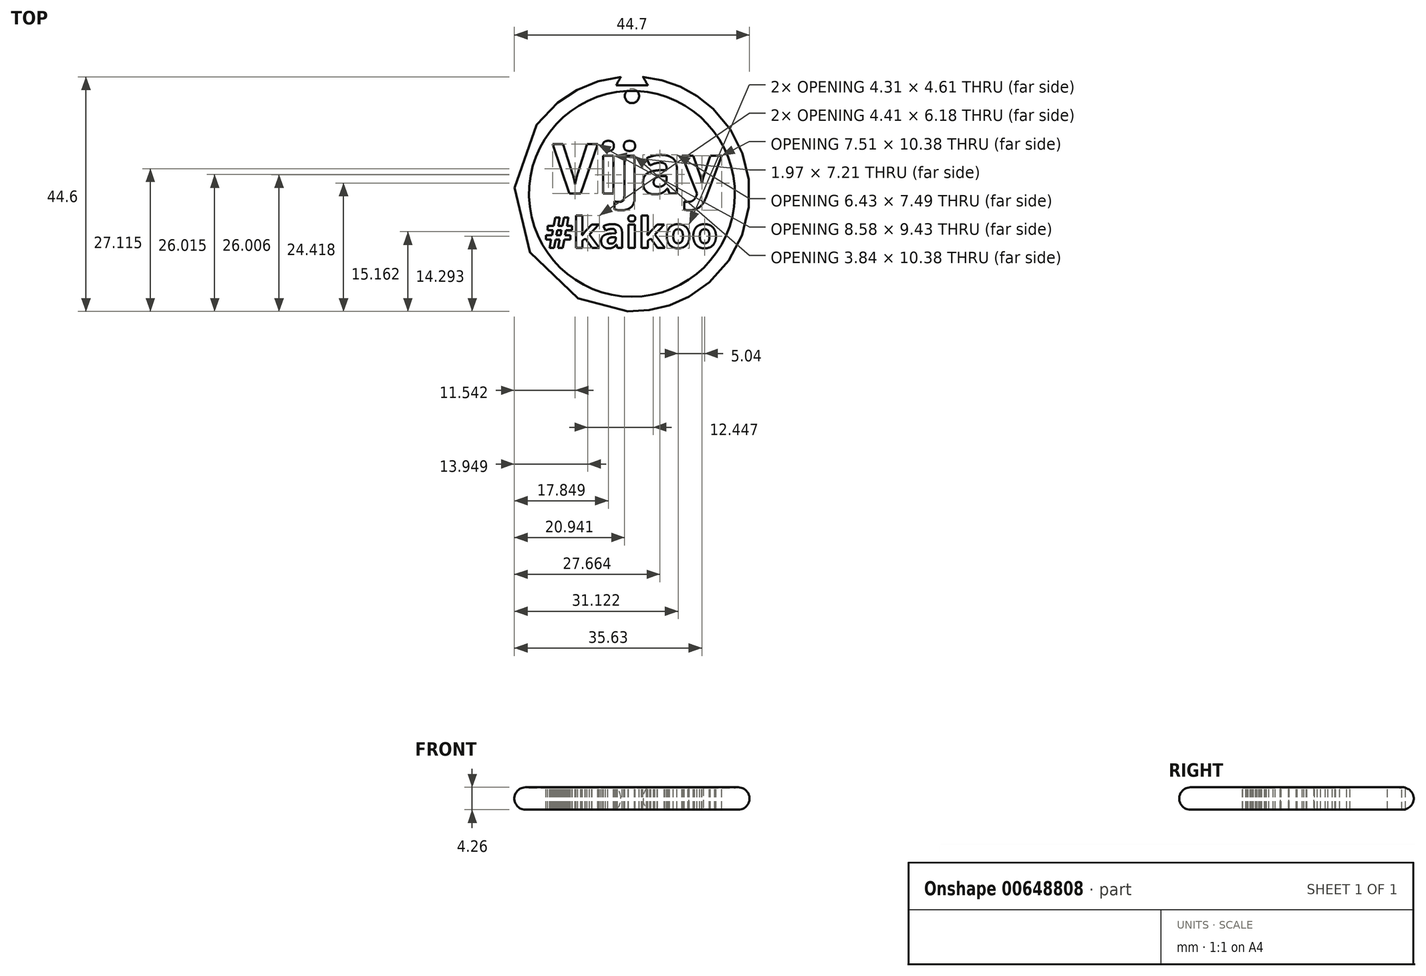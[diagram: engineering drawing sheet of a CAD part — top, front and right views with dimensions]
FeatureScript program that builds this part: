
annotation { "Feature Type Name" : "Feature", "Feature Type Description" : "" }
export const myFeature = defineFeature(function(context is Context, id is Id, definition is map)
    precondition{}
    {
        {
            var Q0;
            Q0=qCreatedBy(makeId("Front.planeOp"),FACE);
            var sketch = newSketch(context, id + "F0", { "sketchPlane" : qUnion([Q0])});
            skLineSegment(sketch, "E0.bottom", {"start": v(0, 0) * mm, "end": v(-19.57, 0) * mm});
            skLineSegment(sketch, "E0.top", {"start": v(0, 4.05) * mm, "end": v(-19.57, 4.05) * mm});
            skLineSegment(sketch, "E0.left", {"start": v(0, 0) * mm, "end": v(0, 4.05) * mm});
            skLineSegment(sketch, "E0.right", {"start": v(-19.57, 0) * mm, "end": v(-19.57, 4.05) * mm});
            skArc(sketch, "E1", {"start": v(-19.57, 4.05) * mm, "mid": v(-22.35, 2.03) * mm, "end": v(-19.57, 0) * mm});
            skSolve(sketch);
        }
        {
            var Q0;
            Q0 = qSketchRegion(id + "F0", true);
            var Q1;
            Q1=sQuery(id+"F0.wireOp",EDGE,"E0.left");
            revolve(context, id + "F1", {"entities" : qUnion([Q0]), "axis" : qUnion([Q1]), "revolveType" : RevolveType.FULL});
        }
        {
            var Q0;
            Q0=makeQuery(id+"F1.opRevolve","SWEPT_FACE",FACE,{"disambiguationData":[OSD([sQuery(id+"F0.wireOp",EDGE,"E0.top")])]});
            var sketch = newSketch(context, id + "F2", { "sketchPlane" : qUnion([Q0])});
            skText(sketch, "E2", { "text": "Vijay", "fontName": "OpenSans-Bold.ttf"});
            skText(sketch, "E3", { "text": "#kaikoo", "fontName": "OpenSans-Bold.ttf"});
            const initialGuessF2  = {"E2": [-0.0151, 5e-05, 1, 0, 0.00951], "E3": [-0.0165, -0.01028, 1, 0, 0.00586]};
            skSetInitialGuess(sketch, initialGuessF2);
            skSolve(sketch);
        }
        {
            var Q0;
            Q0 = qSketchRegion(id + "F2", true);
            extrude(context, id + "F3", {"entities" : qUnion([Q0]), "operationType" : NewBodyOperationType.REMOVE, "oppositeDirection" : true, "depth" : 25.4 * mm, "offsetDistance" : 25.4 * mm});
        }
        {
            var Q0;
            Q0=qCreatedBy(makeId("Top.planeOp"),FACE);
            cPlane(context, id + "F4", {"entities" : qUnion([Q0]), "cplaneType" : CPlaneType.OFFSET, "offset" : 6.35 * mm, "width" : 152.4 * mm, "height" : 152.4 * mm});
        }
        {
            var Q0;
            Q0=qCreatedBy(id+"F4.planeOp",FACE);
            var sketch = newSketch(context, id + "F5", { "sketchPlane" : qUnion([Q0])});
            skCircle(sketch, "E4.cCircle", {"center": v(0, 22.4) * mm, "radius": 1.75 * mm, "construction": true});
            skLineSegment(sketch, "E4.0", {"start": v(3.03, 20.65) * mm, "end": v(-3.03, 20.65) * mm});
            skLineSegment(sketch, "E4.1", {"start": v(-3.03, 20.65) * mm, "end": v(0, 25.9) * mm});
            skLineSegment(sketch, "E4.2", {"start": v(0, 25.9) * mm, "end": v(3.03, 20.65) * mm});
            skPoint(sketch, "E4.0.midPoint", {"position": v(0, 20.65) * mm});
            skSolve(sketch);
        }
        {
            var Q0;
            Q0 = qSketchRegion(id + "F5", true);
            extrude(context, id + "F6", {"entities" : qUnion([Q0]), "operationType" : NewBodyOperationType.REMOVE, "oppositeDirection" : true, "depth" : 25.4 * mm, "offsetDistance" : 25.4 * mm});
        }
        {
            var Q0;
            Q0=makeQuery(id+"F3.boolean.opBoolean","SPLIT",FACE,{"disambiguationData":[TD([makeQuery(id+"F1.opRevolve","SWEPT_FACE",FACE,{"disambiguationData":[OSD([sQuery(id+"F0.wireOp",EDGE,"E1")])]})])],"derivedFrom":makeQuery(id+"F1.opRevolve","SWEPT_FACE",FACE,{"disambiguationData":[OSD([sQuery(id+"F0.wireOp",EDGE,"E0.top")])]})});
            var sketch = newSketch(context, id + "F7", { "sketchPlane" : qUnion([Q0])});
            skCircle(sketch, "E5", {"center": v(0, 18.6) * mm, "radius": 1.36 * mm});
            skSolve(sketch);
        }
        {
            var Q0;
            Q0 = qSketchRegion(id + "F7", true);
            extrude(context, id + "F8", {"entities" : qUnion([Q0]), "operationType" : NewBodyOperationType.REMOVE, "oppositeDirection" : true, "depth" : 25.4 * mm, "offsetDistance" : 25.4 * mm});
        }
    });
